# Revit family: Interceptor_Oil_Integral_Storage_Tank-Zurn-Z1186-ST
name_source: partatom
category: Plumbing Fixtures
units: mm (PartAtom-declared; Revit-internal decimal feet)

## family parameters
Always vertical = Yes
Cut with Voids When Loaded = No
Maintain Annotation Orientation = No
OmniClass Number = 23.45.30.00
OmniClass Title = Washing and Waste Disposal Equipment
Part Type = Normal
Room Calculation Point = No
Round Connector Dimension = Use Radius
Shared = No
Work Plane-Based = No

## types (6) — shared parameters
Assembly Code = D2090300
CW Connection = No
Default Elevation = 25 "
Description = OIL INTERCEPTOR W/ INTEGRAL STORAGE TANK
Extension Box Width = 4.563 "
Extented Box Length = 7 "
HW Connection = No
Manufacturer = Zurn Water, LLC
Manufacurer Brand = Zurn
Model = Z1186-ST
Modified Date = 01/09/2026
Product Documentation Link = https://files.zurn.com
Product Installation Sheet URL = https://files.zurn.com
Product Page URL = https://www.zurn.com
Product data url = https://www.bimobject.com
URL = www.zurn.com
Vent Connection = No
Vent Radius = 0.5 "
WFU = 1
Waste Connection = Yes
zero-valued in all types: CWFU, HWFU

## per-type parameters (varying)
| type | Approx. Weight (Lbs) | Center Lenght of G | Dimension (H) | Dimension (K) | Dimension (N) | Dimension (P) | Height of Body (C) | Inlet/Outlet (D/E) | Inlet/Outlet Connetor Radius | Inlet/Outlet Radius (Actual) | Inlet/Outlet Radius (Inner) | No.of Covers | Oil Storage Tank Capacity Gal (L) | Overall Length (F) | Water Capacity Gal (L) | Width of Body (G) |
| Z1186-ST-300 (2 Inch 10 G.P.M) | 95.00 lbf | 7 " | 12.063 " | 11 " | 16.875 " | 10.125 " | 13.875 " | 8.125 " | 1 " | 1.188 " | 1.034 " | 1 " | 6.00 L | 23.063 " | 7.00 L | 23.563 " |
| Z1186-ST-400 (2 Inch 15 G.P.M) | 95.00 lbf | 7 " | 12.063 " | 11 " | 16.875 " | 10.125 " | 14 " | 8.25 " | 1 " | 1.188 " | 1.034 " | 1 " | 6.00 L | 23.063 " | 9.00 L | 23.563 " |
| Z1186-ST-500 (3 Inch 20 G.P.M) | 115.00 lbf | 8.375 " | 14.188 " | 12.5 " | 18.875 " | 10.313 " | 15.5 " | 9.375 " | 1.5 " | 1.75 " | 1.534 " | 1 " | 8.00 L | 25.063 " | 10.00 L | 26.5 " |
| Z1186-ST-600 (3 Inch 25 G.P.M) | 280.00 lbf | 8.625 " | 19.25 " | 15.25 " | 29 " | 34.188 " | 18.25 " | 11.75 " | 1.5 " | 1.75 " | 1.534 " | 2 " | 55.00 L | 35.219 " | 16.00 L | 50.875 " |
| Z1186-ST-700 (3 Inch 35 G.P.M) | 320.00 lbf | 9.938 " | 23.25 " | 16.75 " | 37 " | 25.688 " | 19.75 " | 12.438 " | 1.5 " | 1.75 " | 1.534 " | 2 " | 55.00 L | 43.438 " | 21.00 L | 45 " |
| Z1186-ST-800 (3 Inch 50 G.P.M) | 529.00 lbf | 9.938 " | 26.25 " | 21.25 " | 43 " | 48.25 " | 24.25 " | 14.188 " | 1.5 " | 1.75 " | 1.534 " | 3 " | 125.00 L | 49.438 " | 30.00 L | 70.125 " |

## geometry (parser evidence)
native form markers: Sweep x3
no freeform markers — native parametric forms only
